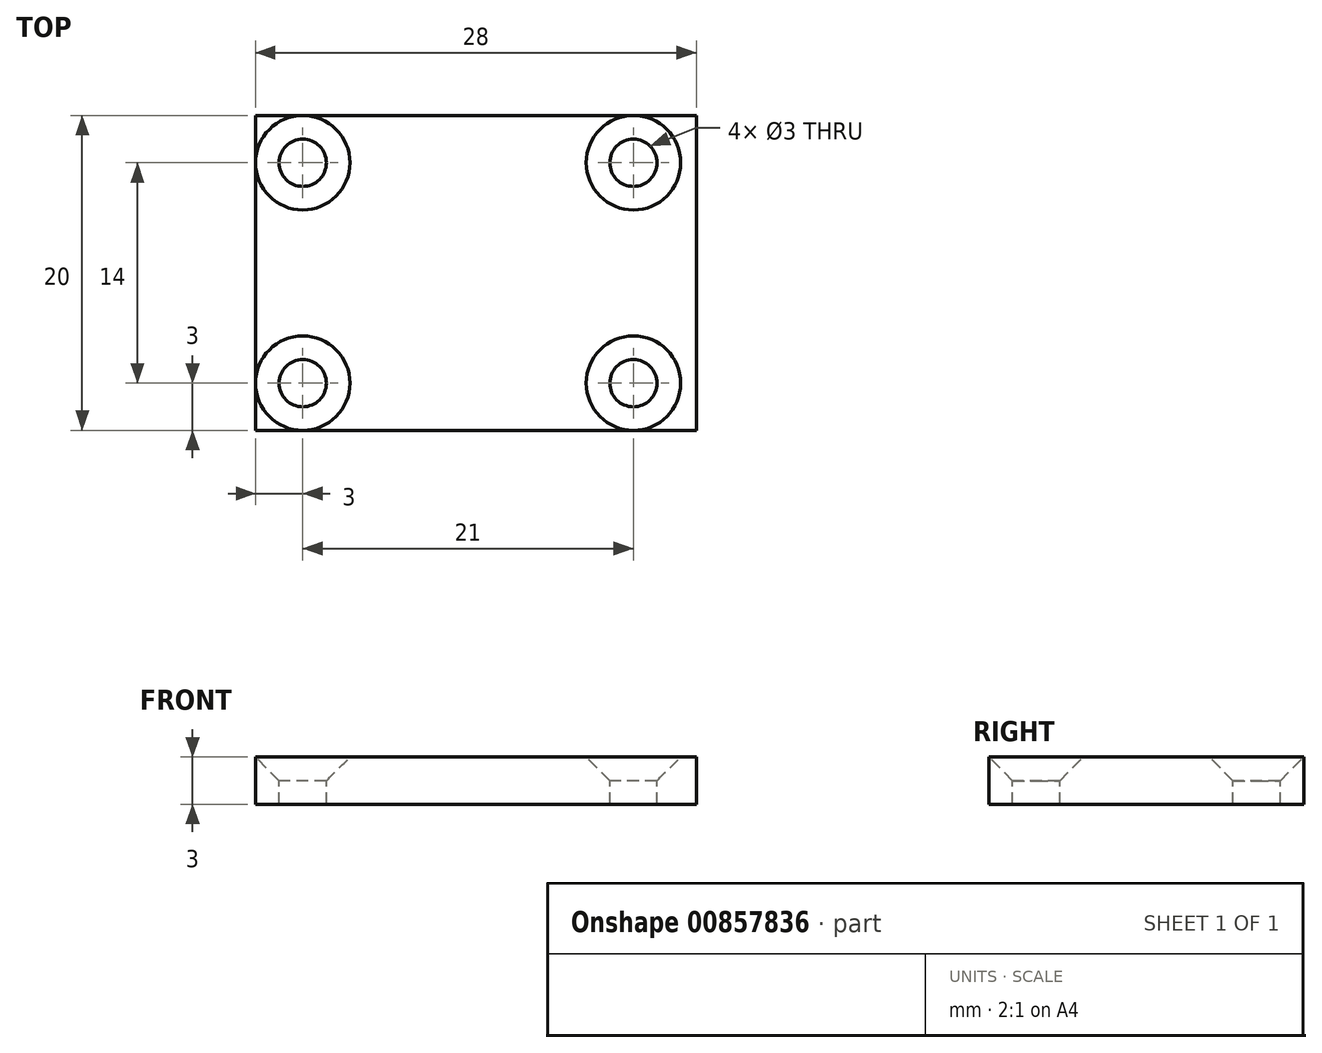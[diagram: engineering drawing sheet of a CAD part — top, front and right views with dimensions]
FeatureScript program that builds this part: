
annotation { "Feature Type Name" : "Feature", "Feature Type Description" : "" }
export const myFeature = defineFeature(function(context is Context, id is Id, definition is map)
    precondition{}
    {
        {
            var Q0;
            Q0=qCreatedBy(makeId("Top.planeOp"),FACE);
            var sketch = newSketch(context, id + "F0", { "sketchPlane" : qUnion([Q0])});
            skLineSegment(sketch, "E0.bottom", {"start": v(-13.5, 10) * mm, "end": v(14.5, 10) * mm});
            skLineSegment(sketch, "E0.top", {"start": v(-13.5, -10) * mm, "end": v(14.5, -10) * mm});
            skLineSegment(sketch, "E0.left", {"start": v(-13.5, 10) * mm, "end": v(-13.5, -10) * mm});
            skLineSegment(sketch, "E0.right", {"start": v(14.5, 10) * mm, "end": v(14.5, -10) * mm});
            skPoint(sketch, "E1", {"position": v(10.5, 7) * mm});
            skPoint(sketch, "E2", {"position": v(10.5, -7) * mm});
            skPoint(sketch, "E3", {"position": v(-10.5, -7) * mm});
            skPoint(sketch, "E4", {"position": v(-10.5, 7) * mm});
            skSolve(sketch);
        }
        {
            var Q0;
            Q0=makeQuery(id+"F0.imprint","IMPRINT",FACE,{"disambiguationData":[TD([[makeQuery(id+"F0.imprint","IMPRINT",EDGE,{"derivedFrom":sQuery(id+"F0.wireOp",EDGE,"E0.bottom")}),-1.0]])]});
            extrude(context, id + "F1", {"entities" : qUnion([Q0]), "oppositeDirection" : true, "depth" : 3 * mm, "offsetDistance" : 25 * mm});
        }
        {
            var Q0;
            Q0=makeQuery(id+"F1.opExtrude","CAP_FACE",FACE,{"disambiguationData":[OSD([sQuery(id+"F0.wireOp",EDGE,"E0.bottom"),sQuery(id+"F0.wireOp",EDGE,"E0.top"),sQuery(id+"F0.wireOp",EDGE,"E0.left"),sQuery(id+"F0.wireOp",EDGE,"E0.right")])],"isStart":true});
            var sketch = newSketch(context, id + "F2", { "sketchPlane" : qUnion([Q0])});
            skPoint(sketch, "E5", {"position": v(-10.5, 7) * mm});
            skPoint(sketch, "E6", {"position": v(10.5, 7) * mm});
            skPoint(sketch, "E7", {"position": v(10.5, -7) * mm});
            skPoint(sketch, "E8", {"position": v(-10.5, -7) * mm});
            skSolve(sketch);
        }
        {
            var Q0;
            Q0=sQuery(id+"F2.wireOp",VERTEX,"E5");
            var Q1;
            Q1=sQuery(id+"F2.wireOp",VERTEX,"E8");
            var Q2;
            Q2=sQuery(id+"F2.wireOp",VERTEX,"E7");
            var Q3;
            Q3=sQuery(id+"F2.wireOp",VERTEX,"E6");
            var Q4;
            Q4=makeQuery(id+"F1.opExtrude","SWEPT_BODY",BODY,{"disambiguationData":[OSD([sQuery(id+"F0.wireOp",EDGE,"E0.bottom"),sQuery(id+"F0.wireOp",EDGE,"E0.top"),sQuery(id+"F0.wireOp",EDGE,"E0.left"),sQuery(id+"F0.wireOp",EDGE,"E0.right")])]});
            hole(context, id + "F3", {"style" : HoleStyle.C_SINK, "endStyle" : HoleEndStyle.THROUGH, "holeDiameter" : 3 * mm, "cSinkDiameter" : 6 * mm, "cSinkAngle" : 90 * degree, "majorDiameter" : 5 * mm, "isTappedThrough" : true, "tappedDepth" : 6 * mm, "tapClearance" : 3, "locations" : qUnion([Q0, Q1, Q2, Q3]), "scope" : qUnion([Q4])});
        }
    });
